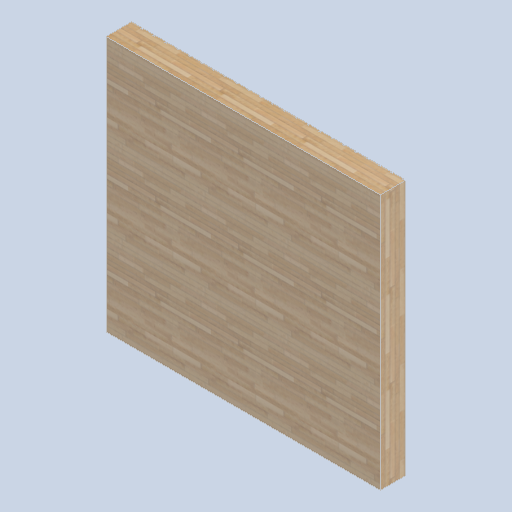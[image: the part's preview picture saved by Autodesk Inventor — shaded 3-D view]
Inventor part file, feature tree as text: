
AUTODESK INVENTOR PART (.ipt)
format: ipt  version: 2024.2 (Build 282272000, 272)  size: 376,832 bytes
history: native  units: in
note: dims shown in document units (in); Inventor stores cm internally (conversion verified against a paired STEP export)
features: other x3, sketch x1
ambient origin geometry x8: Origin, YZ Plane, XZ Plane, XY Plane, X Axis, Y Axis, Z Axis, Center Point
bodies: Solid1 (feature_tree)
feature tree (4):
  other  "front_wall_block05.ipt"
  other  "Solid1::front_wall_block05.ipt"
  other  "TaggingFeature1"
  sketch  "Sketch3"  dims[d0=0.3937in]
